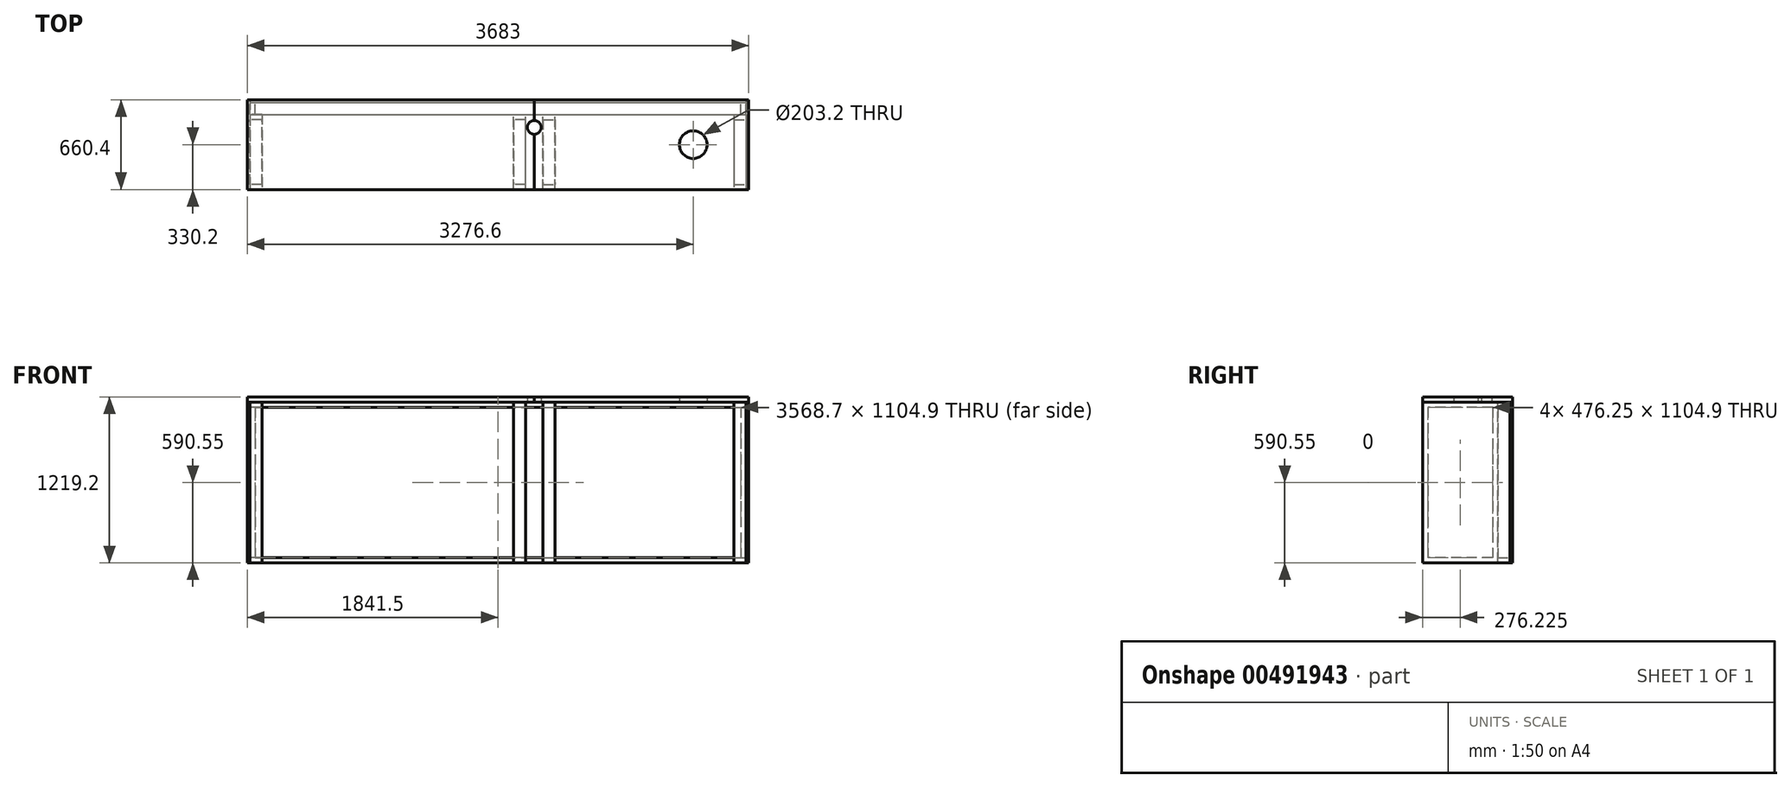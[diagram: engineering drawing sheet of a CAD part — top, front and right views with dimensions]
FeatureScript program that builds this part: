
annotation { "Feature Type Name" : "Feature", "Feature Type Description" : "" }
export const myFeature = defineFeature(function(context is Context, id is Id, definition is map)
    precondition{}
    {
        {
            var Q0;
            Q0=qCreatedBy(makeId("Front.planeOp"),FACE);
            var sketch = newSketch(context, id + "F0", { "sketchPlane" : qUnion([Q0])});
            skLineSegment(sketch, "E0.bottom", {"start": v(0, 0) * mm, "end": v(3644.9, 0) * mm});
            skLineSegment(sketch, "E0.top", {"start": v(0, 1181.1) * mm, "end": v(3644.9, 1181.1) * mm});
            skLineSegment(sketch, "E0.left", {"start": v(0, 0) * mm, "end": v(0, 1181.1) * mm});
            skLineSegment(sketch, "E0.right", {"start": v(3644.9, 0) * mm, "end": v(3644.9, 1181.1) * mm});
            skLineSegment(sketch, "E1.bottom", {"start": v(38.1, 1143) * mm, "end": v(3606.8, 1143) * mm});
            skLineSegment(sketch, "E1.top", {"start": v(38.1, 38.1) * mm, "end": v(3606.8, 38.1) * mm});
            skLineSegment(sketch, "E1.left", {"start": v(38.1, 1143) * mm, "end": v(38.1, 38.1) * mm});
            skLineSegment(sketch, "E1.right", {"start": v(3606.8, 1143) * mm, "end": v(3606.8, 38.1) * mm});
            skLineSegment(sketch, "E2.bottom", {"start": v(901.7, 1143) * mm, "end": v(939.8, 1143) * mm});
            skLineSegment(sketch, "E2.top", {"start": v(901.7, 38.1) * mm, "end": v(939.8, 38.1) * mm});
            skLineSegment(sketch, "E2.left", {"start": v(901.7, 1143) * mm, "end": v(901.7, 38.1) * mm});
            skLineSegment(sketch, "E2.right", {"start": v(939.8, 1143) * mm, "end": v(939.8, 38.1) * mm});
            skLineSegment(sketch, "E3.bottom", {"start": v(2705.1, 1143) * mm, "end": v(2743.2, 1143) * mm});
            skLineSegment(sketch, "E3.top", {"start": v(2705.1, 38.1) * mm, "end": v(2743.2, 38.1) * mm});
            skLineSegment(sketch, "E3.left", {"start": v(2705.1, 1143) * mm, "end": v(2705.1, 38.1) * mm});
            skLineSegment(sketch, "E3.right", {"start": v(2743.2, 1143) * mm, "end": v(2743.2, 38.1) * mm});
            skLineSegment(sketch, "E4.bottom", {"start": v(1803.4, 1143) * mm, "end": v(1841.5, 1143) * mm});
            skLineSegment(sketch, "E4.top", {"start": v(1803.4, 38.1) * mm, "end": v(1841.5, 38.1) * mm});
            skLineSegment(sketch, "E4.left", {"start": v(1803.4, 1143) * mm, "end": v(1803.4, 38.1) * mm});
            skLineSegment(sketch, "E4.right", {"start": v(1841.5, 1143) * mm, "end": v(1841.5, 38.1) * mm});
            skLineSegment(sketch, "E5", {"start": v(1822.45, 0) * mm, "end": v(1822.45, 1181.1) * mm, "construction": true});
            skSolve(sketch);
        }
        {
            var Q0;
            Q0 = qSketchRegion(id + "F0", true);
            var Q1;
            Q1=makeQuery(id+"F0.imprint","IMPRINT",FACE,{"disambiguationData":[TD([[makeQuery(id+"F0.imprint","IMPRINT",EDGE,{"derivedFrom":sQuery(id+"F0.wireOp",EDGE,"E2.bottom")}),-1.0]])]});
            var Q2;
            Q2=makeQuery(id+"F0.imprint","IMPRINT",FACE,{"disambiguationData":[TD([[makeQuery(id+"F0.imprint","IMPRINT",EDGE,{"derivedFrom":sQuery(id+"F0.wireOp",EDGE,"E4.bottom")}),-1.0]])]});
            var Q3;
            Q3=makeQuery(id+"F0.imprint","IMPRINT",FACE,{"disambiguationData":[TD([[makeQuery(id+"F0.imprint","IMPRINT",EDGE,{"derivedFrom":sQuery(id+"F0.wireOp",EDGE,"E3.bottom")}),-1.0]])]});
            extrude(context, id + "F1", {"entities" : qUnion([Q0, Q1, Q2, Q3]), "depth" : 88.9 * mm});
        }
        {
            var Q0;
            Q0=makeQuery(id+"F1.opExtrude","CAP_FACE",FACE,{"disambiguationData":[OSD([sQuery(id+"F0.wireOp",EDGE,"E0.bottom"),sQuery(id+"F0.wireOp",EDGE,"E0.top"),sQuery(id+"F0.wireOp",EDGE,"E0.left"),sQuery(id+"F0.wireOp",EDGE,"E0.right"),sQuery(id+"F0.wireOp",EDGE,"E1.bottom"),sQuery(id+"F0.wireOp",EDGE,"E1.top"),sQuery(id+"F0.wireOp",EDGE,"E1.left"),sQuery(id+"F0.wireOp",EDGE,"E1.right"),sQuery(id+"F0.wireOp",EDGE,"E2.left"),sQuery(id+"F0.wireOp",EDGE,"E2.right"),sQuery(id+"F0.wireOp",EDGE,"E3.left"),sQuery(id+"F0.wireOp",EDGE,"E3.right"),sQuery(id+"F0.wireOp",EDGE,"E4.left"),sQuery(id+"F0.wireOp",EDGE,"E4.right")])],"isStart":true});
            var sketch = newSketch(context, id + "F2", { "sketchPlane" : qUnion([Q0])});
            skLineSegment(sketch, "E6.bottom", {"start": v(-3644.9, 1181.1) * mm, "end": v(0, 1181.1) * mm});
            skLineSegment(sketch, "E6.top", {"start": v(-3644.9, 0) * mm, "end": v(0, 0) * mm});
            skLineSegment(sketch, "E6.left", {"start": v(-3644.9, 1181.1) * mm, "end": v(-3644.9, 0) * mm});
            skLineSegment(sketch, "E6.right", {"start": v(0, 1181.1) * mm, "end": v(0, 0) * mm});
            skSolve(sketch);
        }
        {
            var Q0;
            Q0 = qSketchRegion(id + "F2", true);
            extrude(context, id + "F3", {"entities" : qUnion([Q0]), "depth" : 19.05 * mm});
        }
        {
            var Q0;
            Q0=makeQuery(id+"F3.opExtrude","SWEPT_FACE",FACE,{"disambiguationData":[OSD([sQuery(id+"F2.wireOp",EDGE,"E6.bottom")])]});
            var sketch = newSketch(context, id + "F4", { "sketchPlane" : qUnion([Q0])});
            skCircle(sketch, "E7", {"center": v(2089.15, -184.15) * mm, "radius": 50.8 * mm});
            skCircle(sketch, "E8", {"center": v(3257.55, -311.15) * mm, "radius": 101.6 * mm});
            skLineSegment(sketch, "E9", {"start": v(3257.55, 19.05) * mm, "end": v(3257.55, -641.35) * mm, "construction": true});
            skLineSegment(sketch, "E10.bottom", {"start": v(-19.05, 19.05) * mm, "end": v(3663.95, 19.05) * mm});
            skLineSegment(sketch, "E10.top", {"start": v(-19.05, -641.35) * mm, "end": v(3663.95, -641.35) * mm});
            skLineSegment(sketch, "E10.left", {"start": v(-19.05, 19.05) * mm, "end": v(-19.05, -641.35) * mm});
            skLineSegment(sketch, "E10.right", {"start": v(3663.95, 19.05) * mm, "end": v(3663.95, -641.35) * mm});
            skLineSegment(sketch, "E11", {"start": v(3663.95, -133.35) * mm, "end": v(-19.05, -133.35) * mm, "construction": true});
            skLineSegment(sketch, "E12", {"start": v(2089.15, 19.05) * mm, "end": v(2089.15, -641.35) * mm});
            skSolve(sketch);
        }
        {
            var Q0;
            {var subQ1=sQuery(id+"F2.wireOp",EDGE,"E6.bottom");var subQ2=makeQuery(id+"F3.opExtrude","SWEPT_EDGE",EDGE,{"disambiguationData":[OSD([subQ1,sQuery(id+"F2.wireOp",EDGE,"E6.right")])]});Q0=makeQuery(id+"F4.imprint","IMPRINT",FACE,{"disambiguationData":[TD([[makeQuery(id+"F4.imprint","IMPRINT",EDGE,{"derivedFrom":subQ2}),1.0]])]});}
            var Q1;
            {var subQ0=sQuery(id+"F4.wireOp",EDGE,"E10.left");Q1=makeQuery(id+"F4.imprint","IMPRINT",FACE,{"disambiguationData":[TD([[makeQuery(id+"F4.imprint","IMPRINT",EDGE,{"derivedFrom":subQ0}),1.0]])]});}
            extrude(context, id + "F5", {"entities" : qUnion([Q0, Q1]), "depth" : 38.1 * mm});
        }
        {
            var Q0;
            Q0=makeQuery(id+"F4.imprint","IMPRINT",FACE,{"disambiguationData":[TD([[makeQuery(id+"F4.imprint","IMPRINT",EDGE,{"derivedFrom":sQuery(id+"F4.wireOp",EDGE,"E8")}),-1.0]])]});
            var Q1;
            {var subQ0=sQuery(id+"F4.wireOp",EDGE,"XArBrscS-rBKW-Ltd2-fiZm-o50Mx7gYm2n0.left");var subQ1=sQuery(id+"F4.wireOp",EDGE,"XArBrscS-rBKW-Ltd2-fiZm-o50Mx7gYm2n0.bottom");var subQ2=makeQuery(id+"F4.imprint","INTERSECT",VERTEX,{"derivedFrom":[subQ1,subQ0]});Q1=makeQuery(id+"F4.imprint","IMPRINT",FACE,{"disambiguationData":[TD([[makeQuery(id+"F4.imprint","IMPRINT",EDGE,{"disambiguationData":[TD([[subQ2,1.0]])],"derivedFrom":subQ1}),-1.0]])]});}
            var Q2;
            {var subQ1=sQuery(id+"F2.wireOp",EDGE,"E6.bottom");var subQ2=makeQuery(id+"F3.opExtrude","SWEPT_EDGE",EDGE,{"disambiguationData":[OSD([subQ1,sQuery(id+"F2.wireOp",EDGE,"E6.left")])]});Q2=makeQuery(id+"F4.imprint","IMPRINT",FACE,{"disambiguationData":[TD([[makeQuery(id+"F4.imprint","IMPRINT",EDGE,{"derivedFrom":subQ2}),-1.0]])]});}
            extrude(context, id + "F6", {"entities" : qUnion([Q0, Q1, Q2]), "depth" : 38.1 * mm});
        }
        {
            var Q0;
            Q0=makeQuery(id+"F1.opExtrude","SWEPT_FACE",FACE,{"disambiguationData":[OSD([sQuery(id+"F0.wireOp",EDGE,"E0.left")])]});
            var sketch = newSketch(context, id + "F7", { "sketchPlane" : qUnion([Q0])});
            skLineSegment(sketch, "E13.bottom", {"start": v(88.9, 0) * mm, "end": v(641.35, 0) * mm});
            skLineSegment(sketch, "E13.top", {"start": v(88.9, 1181.1) * mm, "end": v(641.35, 1181.1) * mm});
            skLineSegment(sketch, "E13.left", {"start": v(88.9, 0) * mm, "end": v(88.9, 1181.1) * mm});
            skLineSegment(sketch, "E13.right", {"start": v(641.35, 0) * mm, "end": v(641.35, 1181.1) * mm});
            skLineSegment(sketch, "E14.bottom", {"start": v(603.25, 38.1) * mm, "end": v(127, 38.1) * mm});
            skLineSegment(sketch, "E14.top", {"start": v(603.25, 1143) * mm, "end": v(127, 1143) * mm});
            skLineSegment(sketch, "E14.left", {"start": v(603.25, 38.1) * mm, "end": v(603.25, 1143) * mm});
            skLineSegment(sketch, "E14.right", {"start": v(127, 38.1) * mm, "end": v(127, 1143) * mm});
            skSolve(sketch);
        }
        {
            var Q0;
            Q0=makeQuery(id+"F7.imprint","IMPRINT",FACE,{"disambiguationData":[TD([[makeQuery(id+"F7.imprint","IMPRINT",EDGE,{"derivedFrom":sQuery(id+"F7.wireOp",EDGE,"E13.bottom")}),1.0]])]});
            extrude(context, id + "F8", {"entities" : qUnion([Q0]), "oppositeDirection" : true, "depth" : 88.9 * mm});
        }
        {
            var Q0;
            Q0=makeQuery(id+"F1.opExtrude","SWEPT_FACE",FACE,{"disambiguationData":[OSD([sQuery(id+"F0.wireOp",EDGE,"E0.right")])]});
            var sketch = newSketch(context, id + "F9", { "sketchPlane" : qUnion([Q0])});
            skLineSegment(sketch, "E15.bottom", {"start": v(-88.9, 1181.1) * mm, "end": v(-641.35, 1181.1) * mm});
            skLineSegment(sketch, "E15.top", {"start": v(-88.9, 0) * mm, "end": v(-641.35, 0) * mm});
            skLineSegment(sketch, "E15.left", {"start": v(-88.9, 1181.1) * mm, "end": v(-88.9, 0) * mm});
            skLineSegment(sketch, "E15.right", {"start": v(-641.35, 1181.1) * mm, "end": v(-641.35, 0) * mm});
            skLineSegment(sketch, "E16.bottom", {"start": v(-127, 38.1) * mm, "end": v(-603.25, 38.1) * mm});
            skLineSegment(sketch, "E16.top", {"start": v(-127, 1143) * mm, "end": v(-603.25, 1143) * mm});
            skLineSegment(sketch, "E16.left", {"start": v(-127, 38.1) * mm, "end": v(-127, 1143) * mm});
            skLineSegment(sketch, "E16.right", {"start": v(-603.25, 38.1) * mm, "end": v(-603.25, 1143) * mm});
            skSolve(sketch);
        }
        {
            var Q0;
            Q0=makeQuery(id+"F9.imprint","IMPRINT",FACE,{"disambiguationData":[TD([[makeQuery(id+"F9.imprint","IMPRINT",EDGE,{"derivedFrom":sQuery(id+"F9.wireOp",EDGE,"E15.bottom")}),1.0]])]});
            extrude(context, id + "F10", {"entities" : qUnion([Q0]), "oppositeDirection" : true, "depth" : 88.9 * mm});
        }
        {
            var Q0;
            Q0=makeQuery(id+"F3.opExtrude","SWEPT_FACE",FACE,{"disambiguationData":[OSD([sQuery(id+"F2.wireOp",EDGE,"E6.left")])]});
            var sketch = newSketch(context, id + "F11", { "sketchPlane" : qUnion([Q0])});
            skLineSegment(sketch, "E17.bottom", {"start": v(19.05, 1181.1) * mm, "end": v(-641.35, 1181.1) * mm});
            skLineSegment(sketch, "E17.top", {"start": v(19.05, 0) * mm, "end": v(-641.35, 0) * mm});
            skLineSegment(sketch, "E17.left", {"start": v(19.05, 1181.1) * mm, "end": v(19.05, 0) * mm});
            skLineSegment(sketch, "E17.right", {"start": v(-641.35, 1181.1) * mm, "end": v(-641.35, 0) * mm});
            skSolve(sketch);
        }
        {
            var Q0;
            {var subQ2=sQuery(id+"F11.wireOp",EDGE,"E17.right");Q0=makeQuery(id+"F11.imprint","IMPRINT",FACE,{"disambiguationData":[TD([[makeQuery(id+"F11.imprint","IMPRINT",EDGE,{"derivedFrom":subQ2}),1.0]])]});}
            extrude(context, id + "F12", {"entities" : qUnion([Q0]), "depth" : 19.05 * mm});
        }
        {
            var Q0;
            Q0=makeQuery(id+"F3.opExtrude","SWEPT_FACE",FACE,{"disambiguationData":[OSD([sQuery(id+"F2.wireOp",EDGE,"E6.right")])]});
            var sketch = newSketch(context, id + "F13", { "sketchPlane" : qUnion([Q0])});
            skLineSegment(sketch, "E18.bottom", {"start": v(-19.05, 1181.1) * mm, "end": v(641.35, 1181.1) * mm});
            skLineSegment(sketch, "E18.top", {"start": v(-19.05, 0) * mm, "end": v(641.35, 0) * mm});
            skLineSegment(sketch, "E18.left", {"start": v(-19.05, 1181.1) * mm, "end": v(-19.05, 0) * mm});
            skLineSegment(sketch, "E18.right", {"start": v(641.35, 1181.1) * mm, "end": v(641.35, 0) * mm});
            skSolve(sketch);
        }
        {
            var Q0;
            {var subQ2=sQuery(id+"F13.wireOp",EDGE,"E18.left");Q0=makeQuery(id+"F13.imprint","IMPRINT",FACE,{"disambiguationData":[TD([[makeQuery(id+"F13.imprint","IMPRINT",EDGE,{"derivedFrom":subQ2}),-1.0]])]});}
            var Q1;
            {var subQ2=sQuery(id+"F13.wireOp",EDGE,"E18.right");Q1=makeQuery(id+"F13.imprint","IMPRINT",FACE,{"disambiguationData":[TD([[makeQuery(id+"F13.imprint","IMPRINT",EDGE,{"derivedFrom":subQ2}),-1.0]])]});}
            extrude(context, id + "F14", {"entities" : qUnion([Q0, Q1]), "depth" : 19.05 * mm});
        }
        {
            var Q0;
            Q0=makeQuery(id+"F1.opExtrude","CAP_FACE",FACE,{"disambiguationData":[OSD([sQuery(id+"F0.wireOp",EDGE,"E0.bottom"),sQuery(id+"F0.wireOp",EDGE,"E0.top"),sQuery(id+"F0.wireOp",EDGE,"E0.left"),sQuery(id+"F0.wireOp",EDGE,"E0.right"),sQuery(id+"F0.wireOp",EDGE,"E1.bottom"),sQuery(id+"F0.wireOp",EDGE,"E1.top"),sQuery(id+"F0.wireOp",EDGE,"E1.left"),sQuery(id+"F0.wireOp",EDGE,"E1.right"),sQuery(id+"F0.wireOp",EDGE,"E2.left"),sQuery(id+"F0.wireOp",EDGE,"E2.right"),sQuery(id+"F0.wireOp",EDGE,"E3.left"),sQuery(id+"F0.wireOp",EDGE,"E3.right"),sQuery(id+"F0.wireOp",EDGE,"E4.left"),sQuery(id+"F0.wireOp",EDGE,"E4.right")])],"isStart":false});
            var sketch = newSketch(context, id + "F15", { "sketchPlane" : qUnion([Q0])});
            skLineSegment(sketch, "E19.bottom", {"start": v(2152.65, 0) * mm, "end": v(2241.55, 0) * mm});
            skLineSegment(sketch, "E19.top", {"start": v(2216.15, 1181.1) * mm, "end": v(2241.55, 1181.1) * mm});
            skLineSegment(sketch, "E19.left", {"start": v(2152.65, 0) * mm, "end": v(2152.65, 1181.1) * mm});
            skLineSegment(sketch, "E19.right", {"start": v(2241.55, 0) * mm, "end": v(2241.55, 1181.1) * mm});
            skSolve(sketch);
        }
        {
            var Q0;
            {var subQ0=sQuery(id+"F15.wireOp",EDGE,"E19.top");Q0=makeQuery(id+"F15.imprint","IMPRINT",FACE,{"disambiguationData":[TD([[makeQuery(id+"F15.imprint","IMPRINT",EDGE,{"derivedFrom":subQ0}),-1.0]])]});}
            var Q1;
            {var subQ0=sQuery(id+"F15.wireOp",EDGE,"E19.left");var subQ1=sQuery(id+"F0.wireOp",EDGE,"E3.left");var subQ2=sQuery(id+"F0.wireOp",EDGE,"E1.top");var subQ4=makeQuery(id+"F1.opExtrude","CAP_EDGE",EDGE,{"disambiguationData":[OSD([subQ2]),TDD([makeQuery(id+"F0.imprint","IMPRINT",EDGE,{"disambiguationData":[TD([[makeQuery(id+"F0.imprint","INTERSECT",VERTEX,{"derivedFrom":[subQ2,sQuery(id+"F0.wireOp",EDGE,"E3.top"),subQ1]}),1.0]])],"derivedFrom":subQ2})])],"isStart":false});var subQ5=makeQuery(id+"F15.imprint","INTERSECT",VERTEX,{"derivedFrom":[subQ4,subQ0]});Q1=makeQuery(id+"F15.imprint","IMPRINT",FACE,{"disambiguationData":[TD([[makeQuery(id+"F15.imprint","IMPRINT",EDGE,{"disambiguationData":[TD([[subQ5,-1.0]])],"derivedFrom":subQ0}),-1.0]])]});}
            var Q2;
            {var subQ0=sQuery(id+"F15.wireOp",EDGE,"E19.bottom");Q2=makeQuery(id+"F15.imprint","IMPRINT",FACE,{"disambiguationData":[TD([[makeQuery(id+"F15.imprint","IMPRINT",EDGE,{"derivedFrom":subQ0}),1.0]])]});}
            extrude(context, id + "F16", {"entities" : qUnion([Q0, Q1, Q2]), "depth" : 552.45 * mm});
        }
        {
            var Q0;
            Q0=makeQuery(id+"F16.opExtrude","SWEPT_FACE",FACE,{"disambiguationData":[OSD([sQuery(id+"F15.wireOp",EDGE,"E19.right")])]});
            var sketch = newSketch(context, id + "F17", { "sketchPlane" : qUnion([Q0])});
            skLineSegment(sketch, "E20.bottom", {"start": v(-127, 38.1) * mm, "end": v(-603.25, 38.1) * mm});
            skLineSegment(sketch, "E20.top", {"start": v(-127, 1143) * mm, "end": v(-603.25, 1143) * mm});
            skLineSegment(sketch, "E20.left", {"start": v(-127, 1143) * mm, "end": v(-127, 38.1) * mm});
            skLineSegment(sketch, "E20.right", {"start": v(-603.25, 1143) * mm, "end": v(-603.25, 38.1) * mm});
            skSolve(sketch);
        }
        {
            var Q0;
            Q0=makeQuery(id+"F17.imprint","IMPRINT",FACE,{"disambiguationData":[TD([[makeQuery(id+"F17.imprint","IMPRINT",EDGE,{"derivedFrom":sQuery(id+"F17.wireOp",EDGE,"E20.bottom")}),-1.0]])]});
            var Q1;
            Q1=makeQuery(id+"F16.opExtrude","SWEPT_FACE",FACE,{"disambiguationData":[OSD([sQuery(id+"F15.wireOp",EDGE,"E19.left")])]});
            extrude(context, id + "F18", {"entities" : qUnion([Q0]), "operationType" : NewBodyOperationType.REMOVE, "endBound" : BoundingType.UP_TO_SURFACE, "oppositeDirection" : true, "endBoundEntityFace" : qUnion([Q1]), "depth" : 25.4 * mm});
        }
        {
            var Q0;
            Q0=makeQuery(id+"F1.opExtrude","CAP_FACE",FACE,{"disambiguationData":[OSD([sQuery(id+"F0.wireOp",EDGE,"E0.bottom"),sQuery(id+"F0.wireOp",EDGE,"E0.top"),sQuery(id+"F0.wireOp",EDGE,"E0.left"),sQuery(id+"F0.wireOp",EDGE,"E0.right"),sQuery(id+"F0.wireOp",EDGE,"E1.bottom"),sQuery(id+"F0.wireOp",EDGE,"E1.top"),sQuery(id+"F0.wireOp",EDGE,"E1.left"),sQuery(id+"F0.wireOp",EDGE,"E1.right"),sQuery(id+"F0.wireOp",EDGE,"E2.left"),sQuery(id+"F0.wireOp",EDGE,"E2.right"),sQuery(id+"F0.wireOp",EDGE,"E3.left"),sQuery(id+"F0.wireOp",EDGE,"E3.right"),sQuery(id+"F0.wireOp",EDGE,"E4.left"),sQuery(id+"F0.wireOp",EDGE,"E4.right")])],"isStart":false});
            var sketch = newSketch(context, id + "F19", { "sketchPlane" : qUnion([Q0])});
            skLineSegment(sketch, "E21.bottom", {"start": v(2025.65, 0) * mm, "end": v(1936.75, 0) * mm});
            skLineSegment(sketch, "E21.top", {"start": v(2025.65, 1181.1) * mm, "end": v(1936.75, 1181.1) * mm});
            skLineSegment(sketch, "E21.left", {"start": v(2025.65, 0) * mm, "end": v(2025.65, 1181.1) * mm});
            skLineSegment(sketch, "E21.right", {"start": v(1936.75, 0) * mm, "end": v(1936.75, 1181.1) * mm});
            skSolve(sketch);
        }
        {
            var Q0;
            {var subQ0=sQuery(id+"F19.wireOp",EDGE,"E21.left");var subQ1=sQuery(id+"F0.wireOp",EDGE,"E3.left");var subQ2=sQuery(id+"F0.wireOp",EDGE,"E1.top");var subQ4=makeQuery(id+"F1.opExtrude","CAP_EDGE",EDGE,{"disambiguationData":[OSD([subQ2]),TDD([makeQuery(id+"F0.imprint","IMPRINT",EDGE,{"disambiguationData":[TD([[makeQuery(id+"F0.imprint","INTERSECT",VERTEX,{"derivedFrom":[subQ2,sQuery(id+"F0.wireOp",EDGE,"E3.top"),subQ1]}),1.0]])],"derivedFrom":subQ2})])],"isStart":false});var subQ5=makeQuery(id+"F19.imprint","INTERSECT",VERTEX,{"derivedFrom":[subQ4,subQ0]});Q0=makeQuery(id+"F19.imprint","IMPRINT",FACE,{"disambiguationData":[TD([[makeQuery(id+"F19.imprint","IMPRINT",EDGE,{"disambiguationData":[TD([[subQ5,-1.0]])],"derivedFrom":subQ0}),1.0]])]});}
            var Q1;
            {var subQ0=sQuery(id+"F19.wireOp",EDGE,"E21.top");Q1=makeQuery(id+"F19.imprint","IMPRINT",FACE,{"disambiguationData":[TD([[makeQuery(id+"F19.imprint","IMPRINT",EDGE,{"derivedFrom":subQ0}),-1.0]])]});}
            var Q2;
            {var subQ0=sQuery(id+"F19.wireOp",EDGE,"E21.bottom");Q2=makeQuery(id+"F19.imprint","IMPRINT",FACE,{"disambiguationData":[TD([[makeQuery(id+"F19.imprint","IMPRINT",EDGE,{"derivedFrom":subQ0}),1.0]])]});}
            extrude(context, id + "F20", {"entities" : qUnion([Q0, Q1, Q2]), "depth" : 552.45 * mm});
        }
        {
            var Q0;
            Q0=makeQuery(id+"F20.opExtrude","SWEPT_FACE",FACE,{"disambiguationData":[OSD([sQuery(id+"F19.wireOp",EDGE,"E21.right")])]});
            var sketch = newSketch(context, id + "F21", { "sketchPlane" : qUnion([Q0])});
            skLineSegment(sketch, "E22.bottom", {"start": v(127, 1143) * mm, "end": v(603.25, 1143) * mm});
            skLineSegment(sketch, "E22.top", {"start": v(127, 38.1) * mm, "end": v(603.25, 38.1) * mm});
            skLineSegment(sketch, "E22.left", {"start": v(127, 1143) * mm, "end": v(127, 38.1) * mm});
            skLineSegment(sketch, "E22.right", {"start": v(603.25, 1143) * mm, "end": v(603.25, 38.1) * mm});
            skSolve(sketch);
        }
        {
            var Q0;
            Q0=makeQuery(id+"F21.imprint","IMPRINT",FACE,{"disambiguationData":[TD([[makeQuery(id+"F21.imprint","IMPRINT",EDGE,{"derivedFrom":sQuery(id+"F21.wireOp",EDGE,"E22.bottom")}),-1.0]])]});
            var Q1;
            Q1=makeQuery(id+"F20.opExtrude","SWEPT_FACE",FACE,{"disambiguationData":[OSD([sQuery(id+"F19.wireOp",EDGE,"E21.left")])]});
            extrude(context, id + "F22", {"entities" : qUnion([Q0]), "operationType" : NewBodyOperationType.REMOVE, "endBound" : BoundingType.UP_TO_SURFACE, "oppositeDirection" : true, "endBoundEntityFace" : qUnion([Q1]), "depth" : 25.4 * mm});
        }
    });
